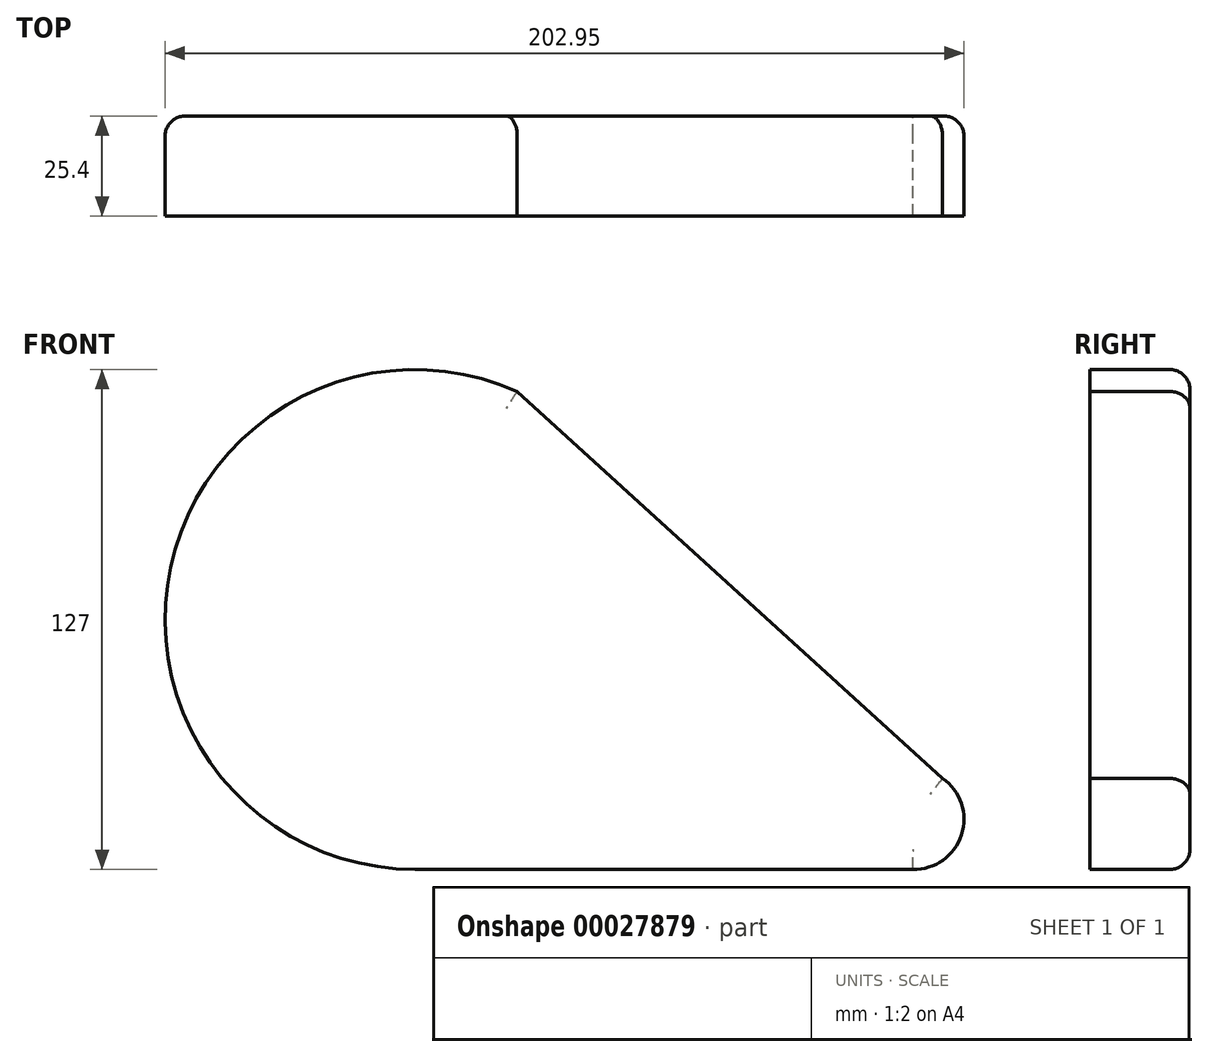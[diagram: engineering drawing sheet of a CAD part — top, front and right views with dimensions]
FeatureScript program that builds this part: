
annotation { "Feature Type Name" : "Feature", "Feature Type Description" : "" }
export const myFeature = defineFeature(function(context is Context, id is Id, definition is map)
    precondition{}
    {
        {
            var Q0;
            Q0=qCreatedBy(makeId("Front.planeOp"),FACE);
            var sketch = newSketch(context, id + "F0", { "sketchPlane" : qUnion([Q0])});
            skCircle(sketch, "E0", {"center": v(0, 0) * mm, "radius": 63.5 * mm});
            skLineSegment(sketch, "E1", {"start": v(0, -63.5) * mm, "end": v(127, -63.5) * mm});
            skCircle(sketch, "E2", {"center": v(126.75, -50.8) * mm, "radius": 12.7 * mm});
            skPoint(sketch, "E2.second.point", {"position": v(127, -38.1) * mm});
            skPoint(sketch, "E2.third.point", {"position": v(136.45, -42.6) * mm});
            skLineSegment(sketch, "E3", {"start": v(25.97, 57.95) * mm, "end": v(136.45, -42.6) * mm});
            skSolve(sketch);
        }
        {
            var Q0;
            {var subQ0=sQuery(id+"F0.wireOp",EDGE,"E2");var subQ1=sQuery(id+"F0.wireOp",EDGE,"E1");var subQ3=makeQuery(id+"F0.imprint","INTERSECT",VERTEX,{"disambiguationData":[OD(0.0)],"derivedFrom":[subQ1,subQ0]});Q0=makeQuery(id+"F0.imprint","IMPRINT",FACE,{"disambiguationData":[TD([[makeQuery(id+"F0.imprint","IMPRINT",EDGE,{"disambiguationData":[TD([[subQ3,1.0]])],"derivedFrom":subQ1}),-1.0]])]});}
            var Q1;
            {var subQ0=sQuery(id+"F0.wireOp",EDGE,"E3");var subQ1=sQuery(id+"F0.wireOp",EDGE,"E2");var subQ3=makeQuery(id+"F0.imprint","INTERSECT",VERTEX,{"disambiguationData":[OD(0.0)],"derivedFrom":[subQ1,subQ0]});Q1=makeQuery(id+"F0.imprint","IMPRINT",FACE,{"disambiguationData":[TD([[makeQuery(id+"F0.imprint","IMPRINT",EDGE,{"disambiguationData":[TD([[subQ3,-1.0]])],"derivedFrom":subQ1}),1.0]])]});}
            var Q2;
            {var subQ3=sQuery(id+"F0.wireOp",EDGE,"E0");var subQ5=sQuery(id+"F0.wireOp",EDGE,"E1");var subQ7=makeQuery(id+"F0.imprint","INTERSECT",VERTEX,{"derivedFrom":[subQ3,subQ5]});Q2=makeQuery(id+"F0.imprint","IMPRINT",FACE,{"disambiguationData":[TD([[makeQuery(id+"F0.imprint","IMPRINT",EDGE,{"disambiguationData":[TD([[subQ7,-1.0]])],"derivedFrom":subQ3}),-1.0]])]});}
            var Q3;
            {var subQ1=sQuery(id+"F0.wireOp",EDGE,"E2");var subQ4=sQuery(id+"F0.wireOp",EDGE,"E1");var subQ5=makeQuery(id+"F0.imprint","INTERSECT",VERTEX,{"disambiguationData":[OD(0.0)],"derivedFrom":[subQ4,subQ1]});Q3=makeQuery(id+"F0.imprint","IMPRINT",FACE,{"disambiguationData":[TD([[makeQuery(id+"F0.imprint","IMPRINT",EDGE,{"disambiguationData":[TD([[subQ5,1.0]])],"derivedFrom":subQ4}),1.0]])]});}
            var Q4;
            {var subQ1=sQuery(id+"F0.wireOp",EDGE,"E0");var subQ4=makeQuery(id+"F0.imprint","INTERSECT",VERTEX,{"derivedFrom":[subQ1,sQuery(id+"F0.wireOp",EDGE,"E1")]});Q4=makeQuery(id+"F0.imprint","IMPRINT",FACE,{"disambiguationData":[TD([[makeQuery(id+"F0.imprint","IMPRINT",EDGE,{"disambiguationData":[TD([[subQ4,1.0]])],"derivedFrom":subQ1}),1.0]])]});}
            extrude(context, id + "F1", {"entities" : qUnion([Q0, Q1, Q2, Q3, Q4]), "depth" : 25.4 * mm});
        }
        {
            var Q0;
            Q0=makeQuery(id+"F1.opExtrude","CAP_FACE",FACE,{"disambiguationData":[OSD([sQuery(id+"F0.wireOp",EDGE,"E0"),sQuery(id+"F0.wireOp",EDGE,"E1"),sQuery(id+"F0.wireOp",EDGE,"E2"),sQuery(id+"F0.wireOp",EDGE,"E3")])],"isStart":true});
            fillet(context, id + "F2", {"entities" : qUnion([Q0]), "radius" : 5.08 * mm, "tangentPropagation" : true, "allowEdgeOverflow" : false});
        }
    });
